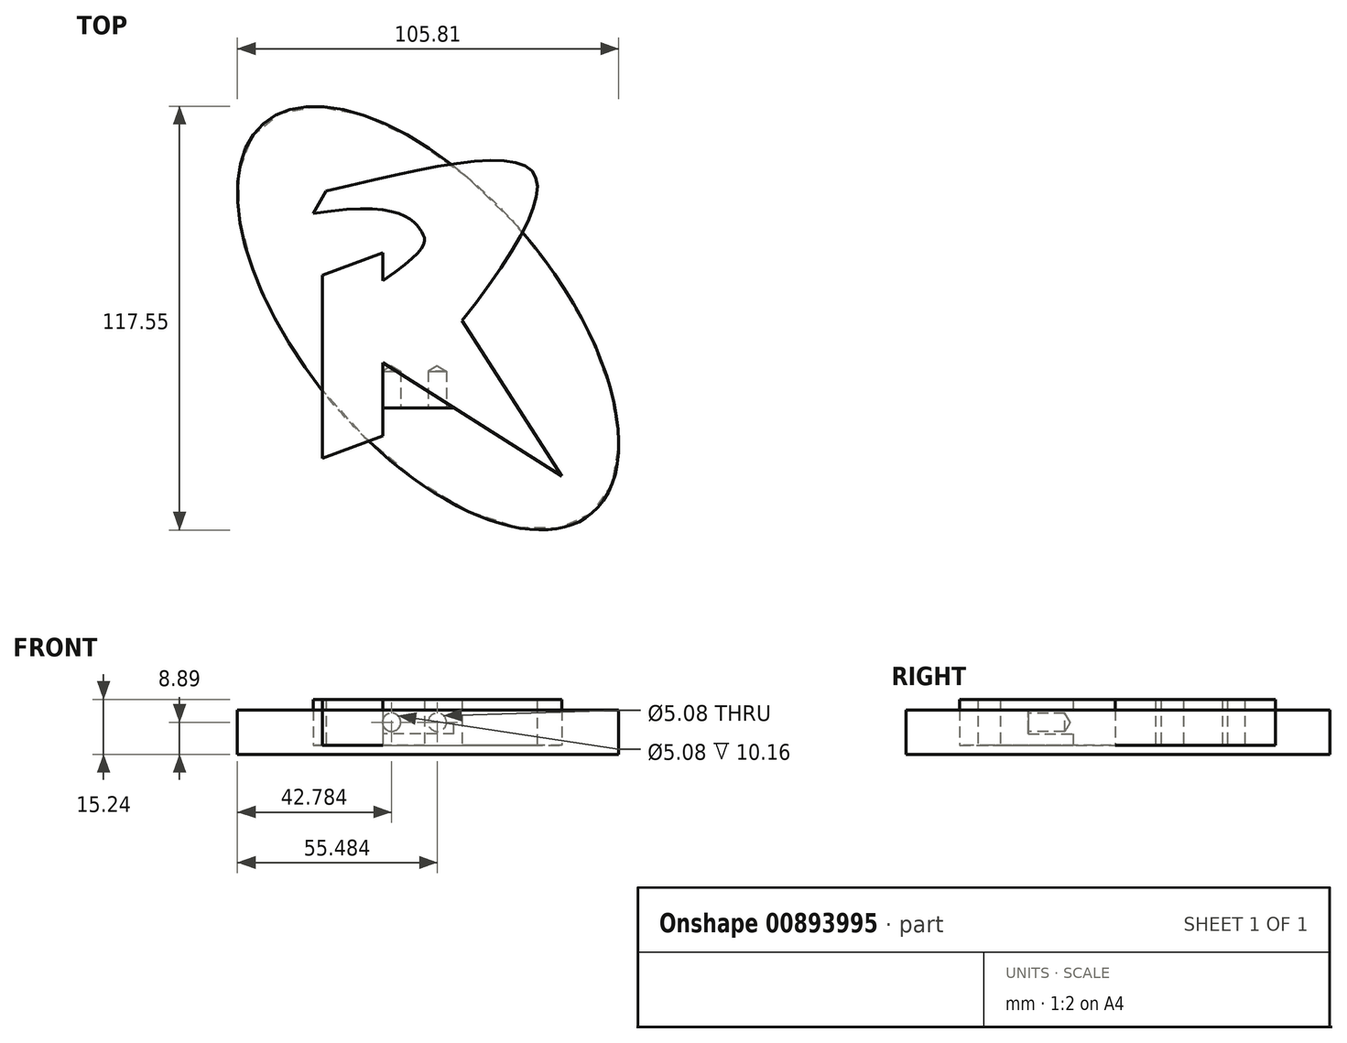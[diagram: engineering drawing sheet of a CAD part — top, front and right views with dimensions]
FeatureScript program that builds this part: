
annotation { "Feature Type Name" : "Feature", "Feature Type Description" : "" }
export const myFeature = defineFeature(function(context is Context, id is Id, definition is map)
    precondition{}
    {
        {
            var Q0;
            Q0=qCreatedBy(makeId("Top.planeOp"),FACE);
            var sketch = newSketch(context, id + "F0", { "sketchPlane" : qUnion([Q0])});
            skLineSegment(sketch, "E0", {"start": v(-17.92, 43) * mm, "end": v(-34.59, 36.83) * mm});
            skLineSegment(sketch, "E1", {"start": v(-34.59, 36.83) * mm, "end": v(-34.59, -13.97) * mm});
            skLineSegment(sketch, "E2", {"start": v(-34.59, -13.97) * mm, "end": v(-17.92, -7.8) * mm});
            skLineSegment(sketch, "E3", {"start": v(-17.92, -7.8) * mm, "end": v(-17.92, 12.53) * mm});
            skLineSegment(sketch, "E4", {"start": v(-17.92, 43) * mm, "end": v(-17.92, 35.28) * mm});
            skLineSegment(sketch, "E5", {"start": v(-17.92, 12.53) * mm, "end": v(31.72, -18.97) * mm});
            skLineSegment(sketch, "E6", {"start": v(31.72, -18.97) * mm, "end": v(4.12, 24.17) * mm});
            skLineSegment(sketch, "E7", {"start": v(-33.68, 60.12) * mm, "end": v(-37.16, 53.89) * mm});
            skFitSpline(sketch, "E8", {"points": [v(-33.68, 60.12) * mm, v(23.7, 65.44) * mm, v(4.12, 24.17) * mm], "startDerivative": vector(153.83, 36.77) * mm, "endDerivative": vector(-92.1, -117.52) * mm});
            skEllipticalArc(sketch, "E9", {});
            skFitSpline(sketch, "E10", {"points": [v(-37.16, 53.89) * mm, v(-7.04, 48.76) * mm, v(-17.92, 35.28) * mm], "startDerivative": vector(120.37, 19.9) * mm, "endDerivative": vector(-86.91, -59.04) * mm});
            const initialGuessF0  = {"E9": [-0.01791688906823568, 0.03528033538854215, 0.80379686513763, 0.5949038574382575, 0.09876497635899556, 0.03513094444578107, 4.410727811812803, 4.454968380384559]};
            skSetInitialGuess(sketch, initialGuessF0);
            skSolve(sketch);
        }
        {
            var Q0;
            Q0=qSketchRegion(id+"F0",true);
            extrude(context, id + "F1", {"entities" : qUnion([Q0]), "endBound" : BoundingType.SYMMETRIC, "depth" : 12.7 * mm, "offsetDistance" : 25.4 * mm});
        }
        {
            var Q0;
            Q0=makeQuery(id+"F1.opExtrude","SWEPT_FACE",FACE,{"disambiguationData":[OSD([sQuery(id+"F0.wireOp",EDGE,"E3")])]});
            var sketch = newSketch(context, id + "F2", { "sketchPlane" : qUnion([Q0])});
            skLineSegment(sketch, "E11.bottom", {"start": v(12.53, 3.42) * mm, "end": v(0, 3.42) * mm});
            skLineSegment(sketch, "E11.top", {"start": v(12.53, -3.28) * mm, "end": v(0, -3.28) * mm});
            skLineSegment(sketch, "E11.left", {"start": v(12.53, 3.42) * mm, "end": v(12.53, -3.28) * mm});
            skLineSegment(sketch, "E11.right", {"start": v(0, 3.42) * mm, "end": v(0, -3.28) * mm});
            skSolve(sketch);
        }
        {
            var Q0;
            Q0=qSketchRegion(id+"F2",true);
            extrude(context, id + "F3", {"entities" : qUnion([Q0]), "operationType" : NewBodyOperationType.ADD, "depth" : 25.4 * mm, "offsetDistance" : 25.4 * mm});
        }
        {
            var Q0;
            Q0=makeQuery(id+"F3.opExtrude","SWEPT_FACE",FACE,{"disambiguationData":[OSD([sQuery(id+"F2.wireOp",EDGE,"E11.right")])]});
            var sketch = newSketch(context, id + "F4", { "sketchPlane" : qUnion([Q0])});
            skPoint(sketch, "E12", {"position": v(-2.77, 0) * mm});
            skPoint(sketch, "E13", {"position": v(-15.47, 0) * mm});
            skSolve(sketch);
        }
        {
            var Q0;
            Q0=sQuery(id+"F4.wireOp",VERTEX,"E13");
            var Q1;
            Q1=sQuery(id+"F4.wireOp",VERTEX,"E12");
            var Q2;
            Q2=makeQuery(id+"F1.opExtrude","SWEPT_BODY",BODY,{"disambiguationData":[OSD([sQuery(id+"F0.wireOp",EDGE,"E0"),sQuery(id+"F0.wireOp",EDGE,"E1"),sQuery(id+"F0.wireOp",EDGE,"E2"),sQuery(id+"F0.wireOp",EDGE,"E3"),sQuery(id+"F0.wireOp",EDGE,"E4"),sQuery(id+"F0.wireOp",EDGE,"E5"),sQuery(id+"F0.wireOp",EDGE,"E6"),sQuery(id+"F0.wireOp",EDGE,"E7"),sQuery(id+"F0.wireOp",EDGE,"E8"),sQuery(id+"F0.wireOp",EDGE,"E10")])]});
            hole(context, id + "F5", {"style" : HoleStyle.SIMPLE, "endStyle" : HoleEndStyle.BLIND, "holeDiameter" : 5.08 * mm, "majorDiameter" : 6.35 * mm, "holeDepth" : 10.16 * mm, "isTappedThrough" : true, "tappedDepth" : 12.7 * mm, "tapClearance" : 3, "locations" : qUnion([Q0, Q1]), "scope" : qUnion([Q2])});
        }
        {
            var Q0;
            Q0=makeQuery(id+"F1.opExtrude","CAP_FACE",FACE,{"disambiguationData":[OSD([sQuery(id+"F0.wireOp",EDGE,"E0"),sQuery(id+"F0.wireOp",EDGE,"E1"),sQuery(id+"F0.wireOp",EDGE,"E2"),sQuery(id+"F0.wireOp",EDGE,"E3"),sQuery(id+"F0.wireOp",EDGE,"E4"),sQuery(id+"F0.wireOp",EDGE,"E5"),sQuery(id+"F0.wireOp",EDGE,"E6"),sQuery(id+"F0.wireOp",EDGE,"E7"),sQuery(id+"F0.wireOp",EDGE,"E8"),sQuery(id+"F0.wireOp",EDGE,"E10")])],"isStart":true});
            var sketch = newSketch(context, id + "F6", { "sketchPlane" : qUnion([Q0])});
            skPoint(sketch, "E14", {"position": v(-5.34, -24.89) * mm});
            skEllipse(sketch, "E15", {"center": v(-5.34, -24.89) * mm, "majorRadius": 70.7 * mm, "minorRadius": 35.4 * mm, "majorAxis": v(0.64, 0.77)});
            skSolve(sketch);
        }
        {
            var Q0;
            Q0 = qSketchRegion(id + "F6", true);
            var Q1;
            Q1=makeQuery(id+"F3.opExtrude","SWEPT_FACE",FACE,{"disambiguationData":[OSD([sQuery(id+"F2.wireOp",EDGE,"E11.bottom")])]});
            extrude(context, id + "F7", {"entities" : qUnion([Q0]), "endBound" : BoundingType.UP_TO_SURFACE, "oppositeDirection" : true, "depth" : 25.4 * mm, "endBoundEntityFace" : qUnion([Q1]), "offsetDistance" : 25.4 * mm, "hasSecondDirection" : true, "secondDirectionOppositeDirection" : false, "secondDirectionDepth" : 2.54 * mm});
        }
    });
